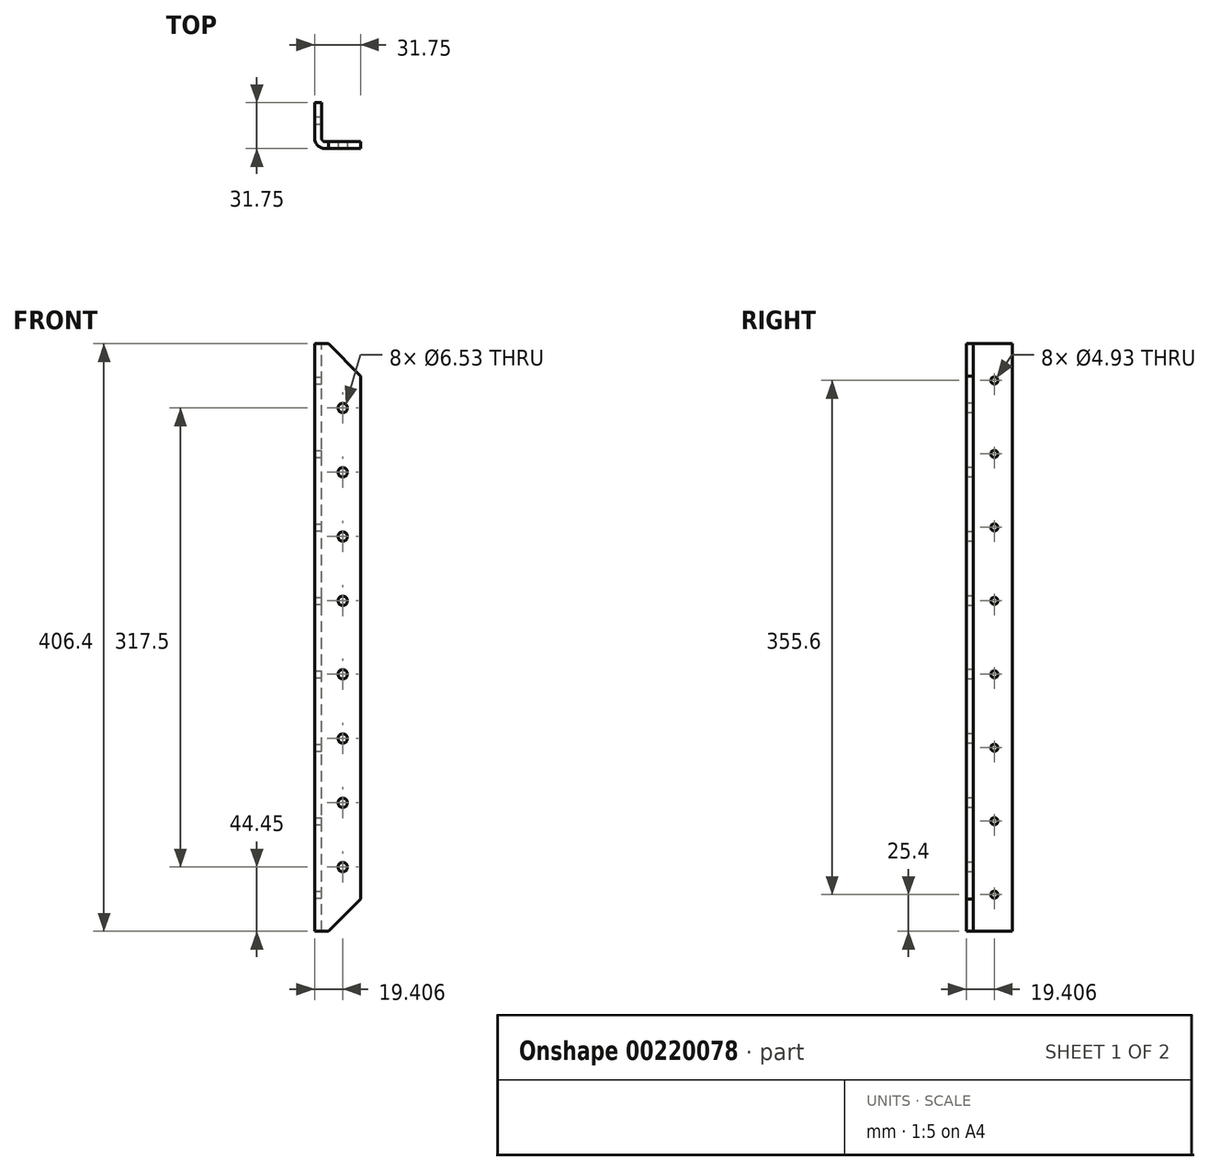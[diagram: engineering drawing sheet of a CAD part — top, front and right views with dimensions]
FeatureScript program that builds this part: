
annotation { "Feature Type Name" : "Feature", "Feature Type Description" : "" }
export const myFeature = defineFeature(function(context is Context, id is Id, definition is map)
    precondition{}
    {
        {
            var Q0;
            Q0=qCreatedBy(makeId("Top.planeOp"),FACE);
            var sketch = newSketch(context, id + "F0", { "sketchPlane" : qUnion([Q0])});
            skLineSegment(sketch, "E0.bottom", {"start": v(7.06, 0) * mm, "end": v(31.75, 0) * mm});
            skLineSegment(sketch, "E0.top", {"start": v(0, 31.75) * mm, "end": v(4.78, 31.75) * mm});
            skLineSegment(sketch, "E0.left", {"start": v(0, 7.06) * mm, "end": v(0, 31.75) * mm});
            skLineSegment(sketch, "E0.right", {"start": v(31.75, 0) * mm, "end": v(31.75, 4.78) * mm});
            skLineSegment(sketch, "E1", {"start": v(4.78, 31.75) * mm, "end": v(4.78, 7.06) * mm});
            skLineSegment(sketch, "E2", {"start": v(7.06, 4.78) * mm, "end": v(31.75, 4.78) * mm});
            skPoint(sketch, "E3.visualSharp", {"position": v(4.78, 4.78) * mm});
            skArc(sketch, "E3.filletArc", {"start": v(4.78, 7.06) * mm, "mid": v(5.44, 5.44) * mm, "end": v(7.06, 4.78) * mm});
            skPoint(sketch, "E4.visualSharp", {"position": v(0, 0) * mm});
            skArc(sketch, "E4.filletArc", {"start": v(0, 7.06) * mm, "mid": v(2.07, 2.07) * mm, "end": v(7.06, 0) * mm});
            skSolve(sketch);
        }
        {
            var Q0;
            Q0 = qSketchRegion(id + "F0", true);
            extrude(context, id + "F1", {"entities" : qUnion([Q0]), "oppositeDirection" : true, "depth" : 406.4 * mm});
        }
        {
            var Q0;
            Q0=makeQuery(id+"F1.opExtrude","CAP_EDGE",EDGE,{"disambiguationData":[OSD([sQuery(id+"F0.wireOp",EDGE,"E0.right")])],"isStart":true});
            var Q1;
            Q1=makeQuery(id+"F1.opExtrude","CAP_EDGE",EDGE,{"disambiguationData":[OSD([sQuery(id+"F0.wireOp",EDGE,"E0.right")])],"isStart":false});
            chamfer(context, id + "F2", {"entities" : qUnion([Q0, Q1]), "width" : 22.35 * mm, "tangentPropagation" : true});
        }
        {
            var Q0;
            Q0=makeQuery(id+"F1.opExtrude","SWEPT_FACE",FACE,{"disambiguationData":[OSD([sQuery(id+"F0.wireOp",EDGE,"E1")])]});
            var sketch = newSketch(context, id + "F3", { "sketchPlane" : qUnion([Q0])});
            skLineSegment(sketch, "E5", {"start": v(19.4, 0) * mm, "end": v(19.4, -406.4) * mm, "construction": true});
            skCircle(sketch, "E6", {"center": v(19.4, -330.2) * mm, "radius": 2.46 * mm});
            skCircle(sketch, "E7", {"center": v(19.4, -76.2) * mm, "radius": 2.46 * mm});
            skCircle(sketch, "E8", {"center": v(19.4, -25.4) * mm, "radius": 2.46 * mm});
            skCircle(sketch, "E9", {"center": v(19.4, -381) * mm, "radius": 2.46 * mm});
            skCircle(sketch, "E10", {"center": v(19.4, -279.4) * mm, "radius": 2.46 * mm});
            skCircle(sketch, "E11", {"center": v(19.4, -228.6) * mm, "radius": 2.46 * mm});
            skCircle(sketch, "E12", {"center": v(19.4, -177.8) * mm, "radius": 2.46 * mm});
            skCircle(sketch, "E13", {"center": v(19.4, -127) * mm, "radius": 2.46 * mm});
            skSolve(sketch);
        }
        {
            var Q0;
            Q0 = qSketchRegion(id + "F3", true);
            extrude(context, id + "F4", {"entities" : qUnion([Q0]), "operationType" : NewBodyOperationType.REMOVE, "oppositeDirection" : true, "depth" : 25.4 * mm});
        }
        {
            var Q0;
            Q0=makeQuery(id+"F1.opExtrude","SWEPT_FACE",FACE,{"disambiguationData":[OSD([sQuery(id+"F0.wireOp",EDGE,"E0.bottom")])]});
            var sketch = newSketch(context, id + "F5", { "sketchPlane" : qUnion([Q0])});
            skLineSegment(sketch, "E14", {"start": v(7.06, -203.2) * mm, "end": v(31.75, -203.2) * mm, "construction": true});
            skLineSegment(sketch, "E15.0", {"start": v(31.75, -384.05) * mm, "end": v(31.75, -22.35) * mm});
            skLineSegment(sketch, "E16.0", {"start": v(31.75, -384.05) * mm, "end": v(31.75, -22.35) * mm, "construction": true});
            skLineSegment(sketch, "E17", {"start": v(19.4, -203.2) * mm, "end": v(19.4, 19.92) * mm, "construction": true});
            skCircle(sketch, "E18", {"center": v(19.4, -177.8) * mm, "radius": 3.26 * mm});
            skCircle(sketch, "E19", {"center": v(19.4, -133.35) * mm, "radius": 3.26 * mm});
            skCircle(sketch, "E20", {"center": v(19.4, -88.9) * mm, "radius": 3.26 * mm});
            skCircle(sketch, "E21", {"center": v(19.4, -44.45) * mm, "radius": 3.26 * mm});
            skLineSegment(sketch, "E22.MirrorCS", {"start": v(19.4, -203.2) * mm, "end": v(19.4, -426.32) * mm, "construction": true});
            skCircle(sketch, "E23.MirrorC", {"center": v(19.4, -361.95) * mm, "radius": 3.26 * mm});
            skCircle(sketch, "E24.MirrorC", {"center": v(19.4, -317.5) * mm, "radius": 3.26 * mm});
            skCircle(sketch, "E25.MirrorC", {"center": v(19.4, -273.05) * mm, "radius": 3.26 * mm});
            skCircle(sketch, "E26.MirrorC", {"center": v(19.4, -228.6) * mm, "radius": 3.26 * mm});
            skSolve(sketch);
        }
        {
            var Q0;
            Q0 = qSketchRegion(id + "F5", true);
            extrude(context, id + "F6", {"entities" : qUnion([Q0]), "operationType" : NewBodyOperationType.REMOVE, "oppositeDirection" : true, "depth" : 25.4 * mm});
        }
    });
